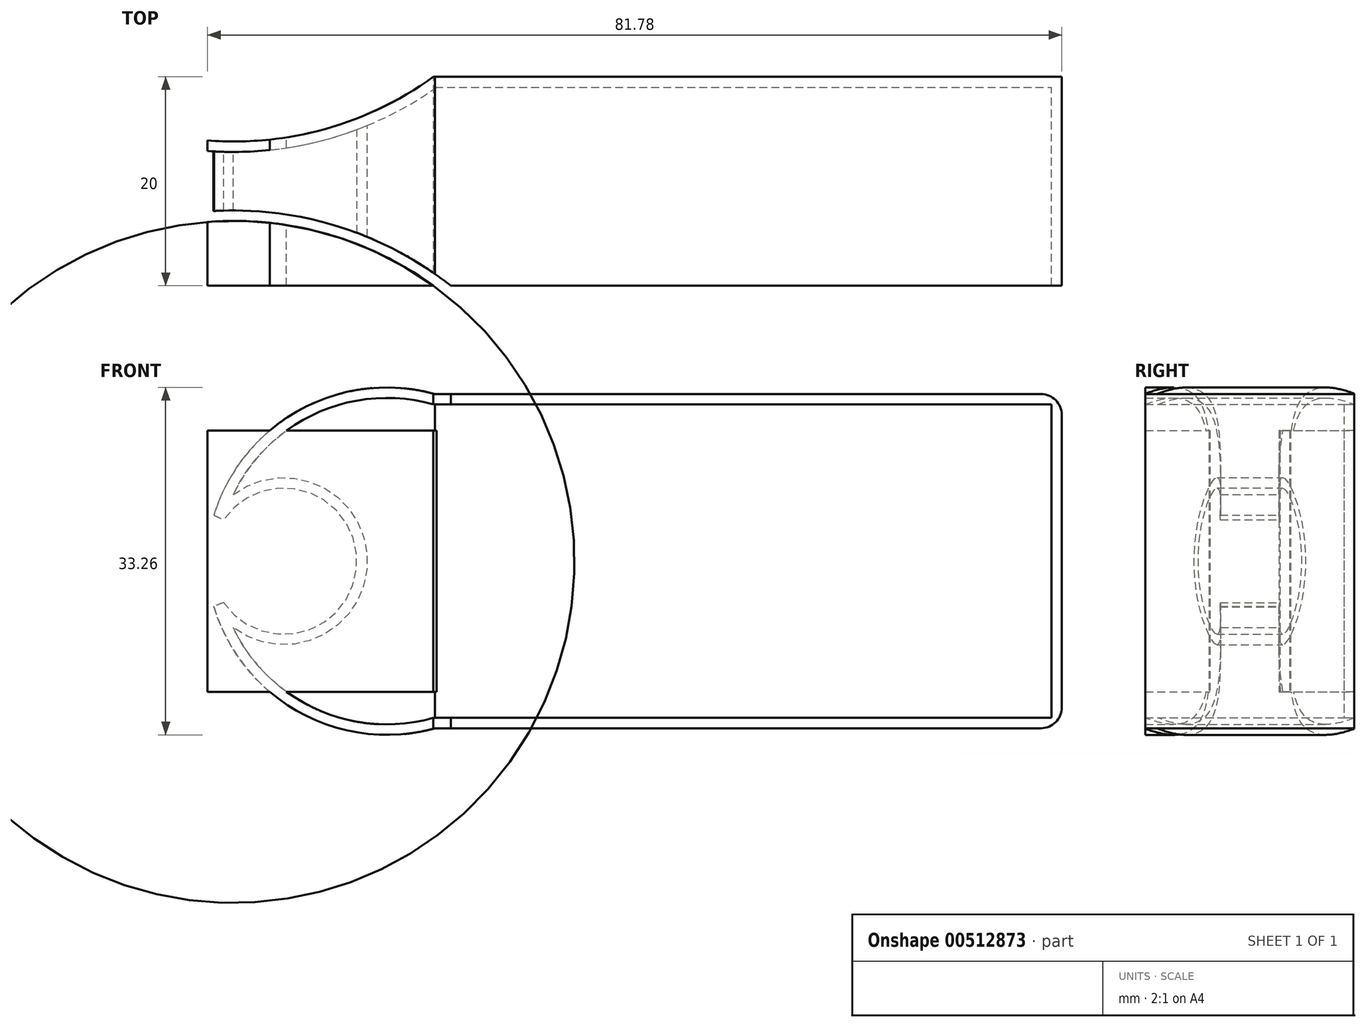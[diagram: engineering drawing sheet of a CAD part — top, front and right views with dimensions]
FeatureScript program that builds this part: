
annotation { "Feature Type Name" : "Feature", "Feature Type Description" : "" }
export const myFeature = defineFeature(function(context is Context, id is Id, definition is map)
    precondition{}
    {
        {
            var Q0;
            Q0=qCreatedBy(makeId("Front.planeOp"),FACE);
            var sketch = newSketch(context, id + "F0", { "sketchPlane" : qUnion([Q0])});
            skLineSegment(sketch, "E0", {"start": v(-81.04, 0) * mm, "end": v(73.56, 0) * mm, "construction": true});
            skLineSegment(sketch, "E1.bottom", {"start": v(-30, 16) * mm, "end": v(30, 16) * mm});
            skLineSegment(sketch, "E1.top", {"start": v(-30, -16) * mm, "end": v(30, -16) * mm});
            skLineSegment(sketch, "E1.right", {"start": v(30, 16) * mm, "end": v(30, -16) * mm});
            skPoint(sketch, "E1.middle", {"position": v(0, 0) * mm});
            skLineSegment(sketch, "E2.0", {"start": v(-30.14, 15) * mm, "end": v(29, 15) * mm});
            skLineSegment(sketch, "E2.2", {"start": v(-30.14, -15) * mm, "end": v(29, -15) * mm});
            skLineSegment(sketch, "E2.3", {"start": v(29, 15) * mm, "end": v(29, -15) * mm});
            skLineSegment(sketch, "E3", {"start": v(-65.3, -8) * mm, "end": v(-44.79, -8) * mm, "construction": true});
            skArc(sketch, "E4", {"start": v(-50.25, -3.96) * mm, "mid": v(-37.48, 0) * mm, "end": v(-50.25, 3.96) * mm});
            skLineSegment(sketch, "E5", {"start": v(0, 16) * mm, "end": v(0, 0) * mm, "construction": true});
            skPoint(sketch, "E5.endSnap0", {"position": v(0, 16) * mm});
            skArc(sketch, "E6.0", {"start": v(-51.2, -4.34) * mm, "mid": v(-51.19, -4.37) * mm, "end": v(-51.17, -4.4) * mm});
            skArc(sketch, "E7", {"start": v(-30, 16) * mm, "mid": v(-42.94, 14.5) * mm, "end": v(-51.17, 4.4) * mm});
            skArc(sketch, "E8.MirrorCS", {"start": v(-30, -16) * mm, "mid": v(-42.94, -14.5) * mm, "end": v(-51.17, -4.4) * mm});
            skLineSegment(sketch, "E9", {"start": v(-51.17, 4.4) * mm, "end": v(-50.25, 3.96) * mm});
            skLineSegment(sketch, "E10", {"start": v(-50.25, -3.96) * mm, "end": v(-51.2, -4.34) * mm});
            skLineSegment(sketch, "E11", {"start": v(-30, 16) * mm, "end": v(-30.14, 15) * mm});
            skLineSegment(sketch, "E12", {"start": v(-30.14, -15) * mm, "end": v(-30, -16) * mm});
            skArc(sketch, "E13.0", {"start": v(-30.14, 15) * mm, "mid": v(-41.31, 14.2) * mm, "end": v(-49.33, 6.37) * mm});
            skArc(sketch, "E14.MirrorCS", {"start": v(-30.14, -15) * mm, "mid": v(-41.31, -14.2) * mm, "end": v(-49.33, -6.37) * mm});
            skPoint(sketch, "E15.orphan", {"position": v(-50.25, 3.96) * mm});
            skArc(sketch, "E16.trimOffspring", {"start": v(-49.33, -6.37) * mm, "mid": v(-36.48, 0) * mm, "end": v(-49.33, 6.37) * mm});
            skSolve(sketch);
        }
        {
            var Q0;
            {var subQ0=sQuery(id+"F0.wireOp",EDGE,"eeea2626-a077-4d98-bbf8-b8026552df01");var subQ1=sQuery(id+"F0.wireOp",EDGE,"XlOoRwsO-9lvs-2DEe-597O-OggXljZX0Xcm");var subQ2=makeQuery(id+"F0.imprint","INTERSECT",VERTEX,{"derivedFrom":[subQ1,subQ0]});Q0=makeQuery(id+"F0.imprint","IMPRINT",FACE,{"disambiguationData":[TD([[makeQuery(id+"F0.imprint","IMPRINT",EDGE,{"disambiguationData":[TD([[subQ2,1.0]])],"derivedFrom":subQ1}),1.0]])]});}
            var Q1;
            {var subQ0=sQuery(id+"F0.wireOp",EDGE,"c10bcea4-8749-4af6-acc7-fa7735835ad4");var subQ1=sQuery(id+"F0.wireOp",EDGE,"8b4c0070-b5bc-40c3-9007-3f364c1a45c6.trimOffspring");var subQ2=makeQuery(id+"F0.imprint","INTERSECT",VERTEX,{"derivedFrom":[subQ1,subQ0]});Q1=makeQuery(id+"F0.imprint","IMPRINT",FACE,{"disambiguationData":[TD([[makeQuery(id+"F0.imprint","IMPRINT",EDGE,{"disambiguationData":[TD([[subQ2,-1.0]])],"derivedFrom":subQ1}),1.0]])]});}
            var Q2;
            {var subQ0=sQuery(id+"F0.wireOp",EDGE,"eeea2626-a077-4d98-bbf8-b8026552df01");var subQ1=sQuery(id+"F0.wireOp",EDGE,"wsCrzJ1f-xYT3-ATGw-PdCk-TVDpaULm4P1I");var subQ2=makeQuery(id+"F0.imprint","INTERSECT",VERTEX,{"derivedFrom":[subQ1,subQ0]});Q2=makeQuery(id+"F0.imprint","IMPRINT",FACE,{"disambiguationData":[TD([[makeQuery(id+"F0.imprint","IMPRINT",EDGE,{"disambiguationData":[TD([[subQ2,1.0]])],"derivedFrom":subQ1}),-1.0]])]});}
            var Q3;
            {var subQ0=sQuery(id+"F0.wireOp",EDGE,"c10bcea4-8749-4af6-acc7-fa7735835ad4");var subQ1=sQuery(id+"F0.wireOp",EDGE,"8a63e338-45c7-4381-bcd9-16bf9e0110d8.trimOffspring");var subQ2=makeQuery(id+"F0.imprint","INTERSECT",VERTEX,{"derivedFrom":[subQ1,subQ0]});Q3=makeQuery(id+"F0.imprint","IMPRINT",FACE,{"disambiguationData":[TD([[makeQuery(id+"F0.imprint","IMPRINT",EDGE,{"disambiguationData":[TD([[subQ2,-1.0]])],"derivedFrom":subQ1}),-1.0]])]});}
            var Q4;
            {var subQ0=sQuery(id+"F0.wireOp",EDGE,"3gMJOj7B-MunL-DJC7-7wsh-2rerEPtw4mEN");var subQ1=sQuery(id+"F0.wireOp",EDGE,"iHZoDJy9-Qb4S-pITb-EAou-BXqFUIZPU52e");var subQ2=makeQuery(id+"F0.imprint","INTERSECT",VERTEX,{"disambiguationData":[OD(0.0)],"derivedFrom":[subQ1,subQ0]});Q4=makeQuery(id+"F0.imprint","IMPRINT",FACE,{"disambiguationData":[TD([[makeQuery(id+"F0.imprint","IMPRINT",EDGE,{"disambiguationData":[TD([[subQ2,1.0]])],"derivedFrom":subQ1}),1.0]])]});}
            var Q5;
            Q5=makeQuery(id+"F0.imprint","IMPRINT",FACE,{"disambiguationData":[TD([[makeQuery(id+"F0.imprint","IMPRINT",EDGE,{"derivedFrom":sQuery(id+"F0.wireOp",EDGE,"E1.bottom")}),-1.0]])]});
            var Q6;
            Q6=makeQuery(id+"F0.imprint","IMPRINT",FACE,{"disambiguationData":[TD([[makeQuery(id+"F0.imprint","IMPRINT",EDGE,{"derivedFrom":sQuery(id+"F0.wireOp",EDGE,"E2.1")}),-1.0]])]});
            var Q7;
            Q7=makeQuery(id+"F0.imprint","IMPRINT",FACE,{"disambiguationData":[TD([[makeQuery(id+"F0.imprint","IMPRINT",EDGE,{"derivedFrom":sQuery(id+"F0.wireOp",EDGE,"E4")}),-1.0]])]});
            extrude(context, id + "F1", {"entities" : qUnion([Q0, Q1, Q2, Q3, Q4, Q5, Q6, Q7]), "depth" : 20 * mm, "offsetDistance" : 25 * mm});
        }
        {
            var Q0;
            Q0=makeQuery(id+"F1.opExtrude","SWEPT_FACE",FACE,{"disambiguationData":[OSD([sQuery(id+"F0.wireOp",EDGE,"E1.right")])]});
            var sketch = newSketch(context, id + "F2", { "sketchPlane" : qUnion([Q0])});
            skLineSegment(sketch, "E17.0", {"start": v(-1, 16) * mm, "end": v(-1, -16) * mm});
            skSolve(sketch);
        }
        {
            var Q0;
            {var subQ0=sQuery(id+"F2.wireOp",EDGE,"E17.0");Q0=makeQuery(id+"F2.imprint","IMPRINT",FACE,{"disambiguationData":[TD([[makeQuery(id+"F2.imprint","IMPRINT",EDGE,{"derivedFrom":subQ0}),1.0]])]});}
            extrude(context, id + "F3", {"entities" : qUnion([Q0]), "operationType" : NewBodyOperationType.ADD, "oppositeDirection" : true, "depth" : 60 * mm, "offsetDistance" : 25 * mm});
        }
        {
            var Q0;
            Q0=makeQuery(id+"F1.opExtrude","SWEPT_EDGE",EDGE,{"disambiguationData":[OSD([sQuery(id+"F0.wireOp",EDGE,"E1.bottom"),sQuery(id+"F0.wireOp",EDGE,"E1.right")])]});
            var Q1;
            Q1=makeQuery(id+"F1.opExtrude","SWEPT_EDGE",EDGE,{"disambiguationData":[OSD([sQuery(id+"F0.wireOp",EDGE,"E1.top"),sQuery(id+"F0.wireOp",EDGE,"E1.right")])]});
            fillet(context, id + "F4", {"entities" : qUnion([Q0, Q1]), "radius" : 2 * mm, "tangentPropagation" : true, "allowEdgeOverflow" : false});
        }
        {
            var Q0;
            Q0=qCreatedBy(makeId("Top.planeOp"),FACE);
            var sketch = newSketch(context, id + "F5", { "sketchPlane" : qUnion([Q0])});
            skArc(sketch, "E18", {"start": v(-51.78, -6.1) * mm, "mid": v(-40.43, -4.97) * mm, "end": v(-30.16, 0) * mm});
            skLineSegment(sketch, "E19", {"start": v(-72.04, -10) * mm, "end": v(71.57, -10) * mm, "construction": true});
            skArc(sketch, "E20.MirrorCS", {"start": v(-51.78, -13.9) * mm, "mid": v(-40.43, -15.03) * mm, "end": v(-30.16, -20) * mm});
            skLineSegment(sketch, "E21.0.1", {"start": v(-30.16, 0) * mm, "end": v(-30.06, -20) * mm, "construction": true});
            skLineSegment(sketch, "E22.0", {"start": v(-51.78, -20) * mm, "end": v(-51.78, 0) * mm, "construction": true});
            skLineSegment(sketch, "E23", {"start": v(-30.16, -20) * mm, "end": v(-51.78, -20) * mm});
            skLineSegment(sketch, "E24", {"start": v(-51.78, -20) * mm, "end": v(-51.78, -13.9) * mm});
            skLineSegment(sketch, "E25", {"start": v(-51.78, -6.1) * mm, "end": v(-51.78, 0) * mm});
            skLineSegment(sketch, "E26.MirrorCS", {"start": v(-30.16, 0) * mm, "end": v(-51.78, 0) * mm});
            skLineSegment(sketch, "E27.MirrorCS", {"start": v(-51.78, 0) * mm, "end": v(-51.78, -20) * mm, "construction": true});
            skArc(sketch, "E28.0", {"start": v(-51.78, -7.1) * mm, "mid": v(-39.48, -5.73) * mm, "end": v(-28.5, 0) * mm});
            skArc(sketch, "E29.MirrorCS", {"start": v(-51.78, -12.9) * mm, "mid": v(-39.48, -14.27) * mm, "end": v(-28.5, -20) * mm});
            skLineSegment(sketch, "E30", {"start": v(-30.16, 0) * mm, "end": v(-28.5, 0) * mm});
            skLineSegment(sketch, "E31", {"start": v(-30.06, -20) * mm, "end": v(-30.16, -20) * mm});
            skLineSegment(sketch, "E32", {"start": v(-30.08, -19.98) * mm, "end": v(-30.16, -20) * mm});
            skLineSegment(sketch, "E33", {"start": v(-28.5, -20) * mm, "end": v(-30.06, -20) * mm});
            skLineSegment(sketch, "E34", {"start": v(-51.78, -6.1) * mm, "end": v(-51.78, -7.1) * mm});
            skLineSegment(sketch, "E35", {"start": v(-51.78, -12.9) * mm, "end": v(-51.78, -13.9) * mm});
            skSolve(sketch);
        }
        {
            var Q0;
            Q0=makeQuery(id+"F5.imprint","IMPRINT",FACE,{"disambiguationData":[TD([[makeQuery(id+"F5.imprint","IMPRINT",EDGE,{"derivedFrom":sQuery(id+"F5.wireOp",EDGE,"E18")}),1.0]])]});
            var Q1;
            Q1=makeQuery(id+"F5.imprint","IMPRINT",FACE,{"disambiguationData":[TD([[makeQuery(id+"F5.imprint","IMPRINT",EDGE,{"derivedFrom":sQuery(id+"F5.wireOp",EDGE,"E20.MirrorCS")}),-1.0]])]});
            extrude(context, id + "F6", {"entities" : qUnion([Q0, Q1]), "operationType" : NewBodyOperationType.REMOVE, "endBound" : BoundingType.SYMMETRIC, "depth" : 38 * mm, "offsetDistance" : 25 * mm});
        }
        {
            var Q0;
            Q0=makeQuery(id+"F5.imprint","IMPRINT",FACE,{"disambiguationData":[TD([[makeQuery(id+"F5.imprint","IMPRINT",EDGE,{"derivedFrom":sQuery(id+"F5.wireOp",EDGE,"E20.MirrorCS")}),1.0]])]});
            var Q1;
            Q1=makeQuery(id+"F5.imprint","IMPRINT",FACE,{"disambiguationData":[TD([[makeQuery(id+"F5.imprint","IMPRINT",EDGE,{"derivedFrom":sQuery(id+"F5.wireOp",EDGE,"E18")}),-1.0]])]});
            extrude(context, id + "F7", {"entities" : qUnion([Q0, Q1]), "operationType" : NewBodyOperationType.ADD, "endBound" : BoundingType.SYMMETRIC, "depth" : 25 * mm, "offsetDistance" : 25 * mm});
        }
    });
